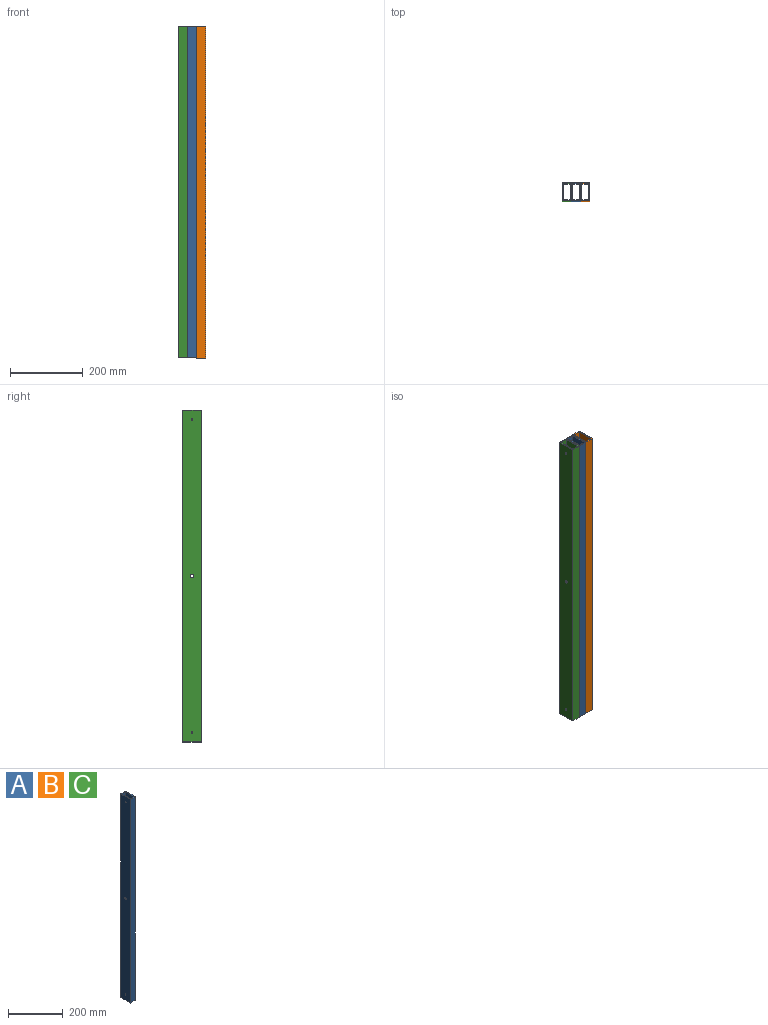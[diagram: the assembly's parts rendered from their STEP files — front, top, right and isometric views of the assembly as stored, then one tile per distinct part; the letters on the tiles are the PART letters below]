
ASSEMBLY  parts=3 mates=3
PART A: 16 faces, bbox 25.4x50.8x914.4 mm
  f0: plane 914.4x19.05mm, normal (0,-1,0), area 17419.3mm2, adj f1,f7,f8,f9
  f1: plane 914.4x44.45mm, normal (-1,0,0), area 40548.3mm2, adj f0,f2,f8,f9,f12,f13,f15
  f2: plane 914.4x19.05mm, normal (0,1,0), area 17419.3mm2, adj f1,f7,f8,f9
  f3: plane 914.4x50.8mm, normal (1,0,0), area 46354.7mm2, adj f4,f6,f8,f9,f12,f13,f15
  f4: plane 914.4x25.4mm, normal (0,1,0), area 23225.8mm2, adj f3,f5,f8,f9
  f5: plane 914.4x50.8mm, normal (-1,0,0), area 46354.7mm2, adj f4,f6,f8,f9,f10,f11,f14
  f6: plane 914.4x25.4mm, normal (0,-1,0), area 23225.8mm2, adj f3,f5,f8,f9
  f7: plane 914.4x44.45mm, normal (1,0,0), area 40548.3mm2, adj f0,f2,f8,f9,f10,f11,f14
  f8: plane 50.8x25.4mm, normal (0,0,1), area 443.5mm2, adj f0,f1,f2,f3,f4,f5,f6,f7
  f9: plane 50.8x25.4mm, normal (0,0,-1), area 443.5mm2, adj f0,f1,f2,f3,f4,f5,f6,f7
  f10: cylinder r=2.55mm len=5.11mm, axis (-1,0,0), area 50.9mm2, adj f5,f7
  f11: cylinder r=2.55mm len=5.11mm, axis (-1,0,0), area 50.9mm2, adj f5,f7
  f12: cylinder r=2.55mm len=5.11mm, axis (-1,0,0), area 50.9mm2, adj f1,f3
  f13: cylinder r=2.55mm len=5.11mm, axis (-1,0,0), area 50.9mm2, adj f1,f3
  f14: cylinder r=4.22mm len=8.43mm, axis (-1,0,0), area 84.1mm2, adj f5,f7
  f15: cylinder r=4.22mm len=8.43mm, axis (-1,0,0), area 84.1mm2, adj f1,f3
PART B: same geometry as A
PART C: same geometry as A
PLACE A t=(12.7,0,-457.2)mm
PLACE B t=(38.1,0,-457.2)mm
PLACE C t=(-12.7,0,-457.2)mm
MATE parallel C.f10 <-> B.f10  axis (1,0,0) through (0,0,431.8)mm
MATE planar A.f14 <-> C.f14  axis (-1,0,0) through (0,0,0)mm
MATE planar A.f14 <-> B.f14  axis (1,0,0) through (25.4,0,0)mm
